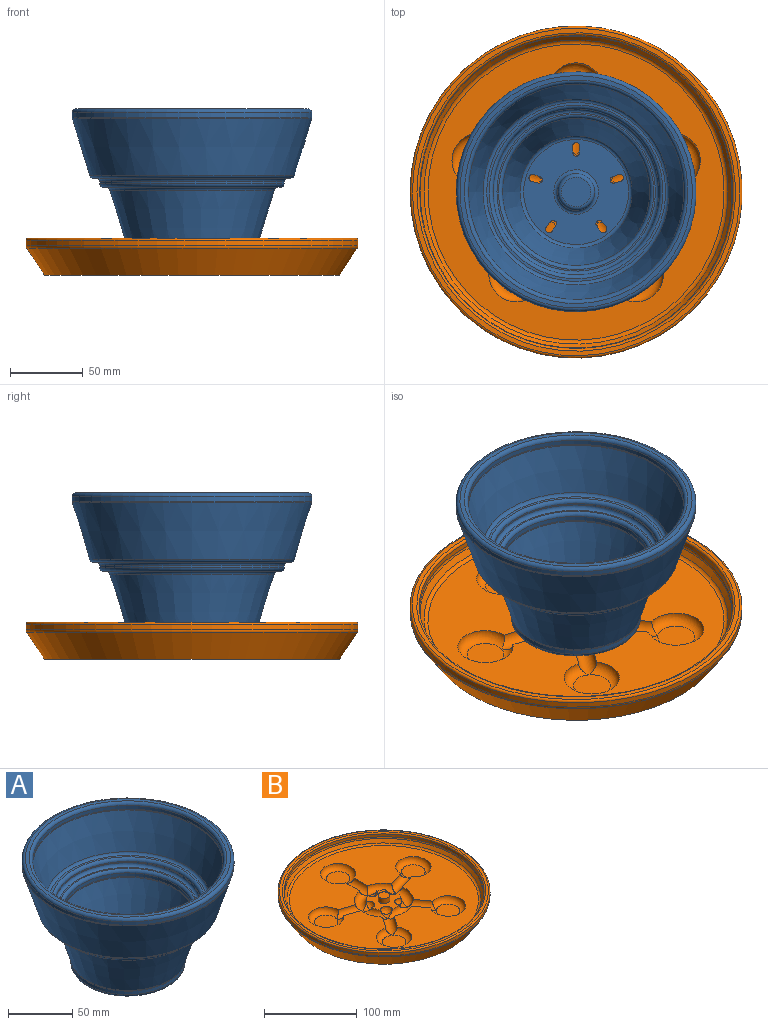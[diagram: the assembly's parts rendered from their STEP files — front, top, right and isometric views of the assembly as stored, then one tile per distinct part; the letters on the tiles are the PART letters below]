
ASSEMBLY  parts=2 mates=1
PART A: 59 faces, bbox 178.7x178.7x101.6 mm
  f0: plane 12.7x12.7mm, normal (0,0,-1), area 126.7mm2, adj f1
  f1: cylinder r=6.35mm len=12.7mm, axis (0,0,-1), area 253.4mm2, adj f0,f2
  f2: plane 83.62x83.62mm, normal (0,0,-1), area 5165mm2, adj f1,f3,f39,f40,f41,f42,f43,f44
  f3: torus R=41.81mm, axis (0,0,-1), area 1133.7mm2, adj f2,f4
  f4: cylinder r=44.45mm len=88.9mm, axis (0,0,-1), area 924.9mm2, adj f3,f5
  f5: torus R=47.09mm, axis (0,0,-1), area 220.4mm2, adj f4,f6
  f6: cone r=44.57mm half-angle=17.1deg, axis (0,0,1), area 12975.9mm2, adj f5,f7
  f7: torus R=59.1mm, axis (0,0,-1), area 1216.9mm2, adj f6,f8
  f8: plane 121.72x121.72mm, normal (0,0,-1), area 662.6mm2, adj f7,f9
  f9: torus R=60.86mm, axis (0,0,-1), area 1630.3mm2, adj f8,f10
  f10: cylinder r=63.5mm len=127mm, axis (0,0,-1), area 425.9mm2, adj f9,f11
  f11: torus R=66.14mm, axis (0,0,-1), area 1680.3mm2, adj f10,f12
  f12: cone r=67.9mm half-angle=90deg, axis (0,0,1), area 740.4mm2, adj f11,f13
  f13: torus R=67.9mm, axis (0,0,-1), area 1464.5mm2, adj f12,f14
  f14: cone r=70.42mm half-angle=17.1deg, axis (0,0,1), area 19610.4mm2, adj f13,f15
  f15: torus R=79.91mm, axis (0,0,-1), area 408.7mm2, adj f14,f16
  f16: cylinder r=82.55mm len=165.1mm, axis (0,0,-1), area 1717.7mm2, adj f15,f17
  f17: torus R=79.91mm, axis (0,0,-1), area 2126.8mm2, adj f16,f18
  f18: plane 159.82x159.82mm, normal (0,0,1), area 1477.1mm2, adj f17,f19
  f19: torus R=76.91mm, axis (0,0,-1), area 1961mm2, adj f18,f20
  f20: cylinder r=74.27mm len=148.54mm, axis (0,0,-1), area 1545.4mm2, adj f19,f21
  f21: torus R=71.63mm, axis (0,0,-1), area 367.7mm2, adj f20,f22
  f22: cone r=74.15mm half-angle=17.1deg, axis (0,0,1), area 14853.6mm2, adj f21,f23
  f23: torus R=61.57mm, axis (0,0,-1), area 1330.9mm2, adj f22,f24
  f24: cone r=59.8mm half-angle=90deg, axis (0,0,1), area 674.1mm2, adj f23,f25
  f25: torus R=59.8mm, axis (0,0,-1), area 1515.1mm2, adj f24,f26
  f26: cone r=57.16mm half-angle=0deg, axis (0,0,-1), area 381mm2, adj f25,f27
  f27: torus R=54.52mm, axis (0,0,-1), area 1465mm2, adj f26,f28
  f28: cone r=53.44mm half-angle=90deg, axis (0,0,1), area 366.1mm2, adj f27,f29
  f29: torus R=53.44mm, axis (0,0,-1), area 1349.2mm2, adj f28,f30
  f30: cone r=50.8mm half-angle=0deg, axis (0,0,-1), area 1057mm2, adj f29,f31
  f31: torus R=48.16mm, axis (0,0,-1), area 251.5mm2, adj f30,f32
  f32: cone r=38.67mm half-angle=17.1deg, axis (0,0,1), area 11463.8mm2, adj f31,f33
  f33: torus R=36.15mm, axis (0,0,-1), area 794.2mm2, adj f32,f34
  f34: plane 72.3x72.3mm, normal (0,0,1), area 3166.2mm2, adj f33,f35,f39,f40,f41,f42,f43,f44
  f35: torus R=15.34mm, axis (0,0,-1), area 356.1mm2, adj f34,f36
  f36: cylinder r=12.7mm len=25.4mm, axis (0,0,-1), area 85.2mm2, adj f35,f37
  f37: torus R=10.06mm, axis (0,0,-1), area 306mm2, adj f36,f38
  f38: plane 20.12x20.12mm, normal (0,0,1), area 317.9mm2, adj f37
  f39: cylinder r=2.54mm len=6.35mm, axis (0,0,1), area 50.7mm2, adj f2,f34,f40,f41
  f40: plane 6.35x4.64mm, normal (-0.24,0.97,0), area 30.4mm2, adj f2,f34,f39,f42
  f41: plane 6.35x4.44mm, normal (0.37,-0.93,0), area 30.4mm2, adj f2,f34,f39,f42
  f42: cylinder r=2.22mm len=6.35mm, axis (0,0,1), area 42.4mm2, adj f2,f34,f40,f41
  f43: cylinder r=2.54mm len=6.35mm, axis (0,0,1), area 50.7mm2, adj f2,f34,f44,f45
  f44: plane 6.35x4.05mm, normal (0.85,0.53,0), area 30.4mm2, adj f2,f34,f43,f46
  f45: plane 6.35x3.67mm, normal (-0.77,-0.64,0), area 30.4mm2, adj f2,f34,f43,f46
  f46: cylinder r=2.22mm len=6.35mm, axis (0,0,1), area 42.4mm2, adj f2,f34,f44,f45
  f47: cylinder r=2.54mm len=6.35mm, axis (0,0,1), area 50.7mm2, adj f2,f34,f48,f49
  f48: plane 6.35x3.67mm, normal (0.77,-0.64,0), area 30.4mm2, adj f2,f34,f47,f50
  f49: plane 6.35x4.05mm, normal (-0.85,0.53,0), area 30.4mm2, adj f2,f34,f47,f50
  f50: cylinder r=2.22mm len=6.35mm, axis (0,0,1), area 42.4mm2, adj f2,f34,f48,f49
  f51: cylinder r=2.54mm len=6.35mm, axis (0,0,1), area 50.7mm2, adj f2,f34,f52,f53
  f52: plane 6.35x4.44mm, normal (-0.37,-0.93,0), area 30.4mm2, adj f2,f34,f51,f54
  f53: plane 6.35x4.64mm, normal (0.24,0.97,0), area 30.4mm2, adj f2,f34,f51,f54
  f54: cylinder r=2.22mm len=6.35mm, axis (0,0,1), area 42.4mm2, adj f2,f34,f52,f53
  f55: cylinder r=2.54mm len=6.35mm, axis (0,0,1), area 50.7mm2, adj f2,f34,f56,f57
  f56: plane 6.35x4.78mm, normal (-1,0.07,0), area 30.4mm2, adj f2,f34,f55,f58
  f57: plane 6.35x4.78mm, normal (1,0.07,0), area 30.4mm2, adj f2,f34,f55,f58
  f58: cylinder r=2.22mm len=6.35mm, axis (0,0,1), area 42.4mm2, adj f2,f34,f56,f57
PART B: 50 faces, bbox 247.4x247.4x25.4 mm
  f0: plane 203.88x203.88mm, normal (0,0,1), area 22533mm2, adj f1,f2,f3,f4,f5,f6,f7,f8
  f1: torus R=25.4mm, axis (0,0,-1), area 474.1mm2, adj f0,f19,f35,f37,f47,f49
  f2: torus R=25.4mm, axis (0,0,-1), area 474.1mm2, adj f0,f19,f44,f46,f47,f49
  f3: torus R=12.7mm, axis (0,0,-1), area 967.5mm2, adj f0,f30,f47
  f4: torus R=25.4mm, axis (0,0,-1), area 474.1mm2, adj f0,f19,f41,f43,f44,f46
  f5: torus R=12.7mm, axis (0,0,1), area 967.5mm2, adj f0,f32,f44
  f6: torus R=25.4mm, axis (0,0,-1), area 474.1mm2, adj f0,f19,f38,f40,f41,f43
  f7: torus R=12.7mm, axis (0,0,1), area 967.5mm2, adj f0,f34,f41
  f8: torus R=25.4mm, axis (0,0,-1), area 474.1mm2, adj f0,f19,f35,f37,f38,f40
  f9: torus R=12.7mm, axis (0,0,1), area 967.5mm2, adj f0,f33,f38
  f10: torus R=12.7mm, axis (0,0,1), area 967.5mm2, adj f0,f31,f35
  f11: cylinder r=114.3mm len=228.6mm, axis (0,0,-1), area 2672mm2, adj f12,f22
  f12: torus R=112.68mm, axis (0,0,-1), area 1822.5mm2, adj f11,f13
  f13: plane 225.35x225.35mm, normal (0,0,1), area 2165.9mm2, adj f12,f14
  f14: torus R=109.57mm, axis (0,0,-1), area 1739.7mm2, adj f13,f15
  f15: cylinder r=107.95mm len=215.9mm, axis (0,0,-1), area 2523.6mm2, adj f14,f16
  f16: torus R=104.63mm, axis (0,0,-1), area 1322.1mm2, adj f15,f17
  f17: cone r=107.39mm half-angle=33.7deg, axis (0,0,1), area 3231mm2, adj f16,f18
  f18: torus R=101.94mm, axis (0,0,-1), area 2121.2mm2, adj f0,f17
  f19: plane 38.09x37.01mm, normal (0,0,1), area 670mm2, adj f1,f2,f4,f6,f8,f23,f25,f26
  f20: plane 203.2x203.2mm, normal (0,0,-1), area 32429.3mm2, adj f21
  f21: cone r=113.74mm half-angle=33.7deg, axis (0,0,1), area 14808.8mm2, adj f20,f22
  f22: torus R=110.98mm, axis (0,0,-1), area 1400mm2, adj f11,f21
  f23: cylinder r=6.35mm len=12.7mm, axis (0,0,-1), area 253.4mm2, adj f19,f24
  f24: plane 12.7x12.7mm, normal (0,0,1), area 126.7mm2, adj f23
  f25: revolved ~12.3x8.01mm, area 117.1mm2, adj f19,f48
  f26: revolved ~12.7x6.04mm, area 117.1mm2, adj f19,f36
  f27: revolved ~11.31x9.83mm, area 117.1mm2, adj f19,f45
  f28: revolved ~11.31x9.83mm, area 117.1mm2, adj f19,f42
  f29: revolved ~12.3x8.01mm, area 117.1mm2, adj f19,f39
  f30: plane 25.4x25.4mm, normal (0,0,1), area 506.7mm2, adj f3
  f31: plane 25.4x25.4mm, normal (0,0,1), area 506.7mm2, adj f10
  f32: plane 25.4x25.4mm, normal (0,0,1), area 506.7mm2, adj f5
  f33: plane 25.4x25.4mm, normal (0,0,1), area 506.7mm2, adj f9
  f34: plane 25.4x25.4mm, normal (0,0,1), area 506.7mm2, adj f7
  f35: cylinder r=6.35mm len=31.75mm, axis (0,1,0), area 490.1mm2, adj f0,f1,f8,f10
  f36: plane 12.7x6.35mm, normal (0,1,0), area 3.9mm2, adj f26,f37
  f37: cylinder r=6.35mm len=12.7mm, axis (0,1,0), area 57.5mm2, adj f1,f8,f36
  f38: cylinder r=6.35mm len=34.12mm, axis (0.95,0.31,0), area 490.1mm2, adj f0,f6,f8,f9
  f39: plane 12.08x6.35mm, normal (0.95,0.31,0), area 3.9mm2, adj f29,f40
  f40: cylinder r=6.35mm len=14.38mm, axis (0.95,0.31,0), area 57.5mm2, adj f6,f8,f39
  f41: cylinder r=6.35mm len=33.15mm, axis (0.59,-0.81,0), area 490.1mm2, adj f0,f4,f6,f7
  f42: plane 10.27x7.47mm, normal (0.59,-0.81,0), area 3.9mm2, adj f28,f43
  f43: cylinder r=6.35mm len=14.65mm, axis (0.59,-0.81,0), area 57.5mm2, adj f4,f6,f42
  f44: cylinder r=6.35mm len=33.15mm, axis (-0.59,-0.81,0), area 490.1mm2, adj f0,f2,f4,f5
  f45: plane 10.27x7.47mm, normal (-0.59,-0.81,0), area 3.9mm2, adj f27,f46
  f46: cylinder r=6.35mm len=14.65mm, axis (-0.59,-0.81,0), area 57.5mm2, adj f2,f4,f45
  f47: cylinder r=6.35mm len=34.12mm, axis (-0.95,0.31,0), area 490.1mm2, adj f0,f1,f2,f3
  f48: plane 12.08x6.35mm, normal (-0.95,0.31,0), area 3.9mm2, adj f25,f49
  f49: cylinder r=6.35mm len=14.38mm, axis (-0.95,0.31,0), area 57.5mm2, adj f1,f2,f48
PLACE A t=(65.87,74.53,3.95)mm
PLACE B t=(65.87,74.53,-8.75)mm
MATE fastened B.f1 <-> A.f1  axis (0,0,1) through (65.87,74.53,3.95)mm
